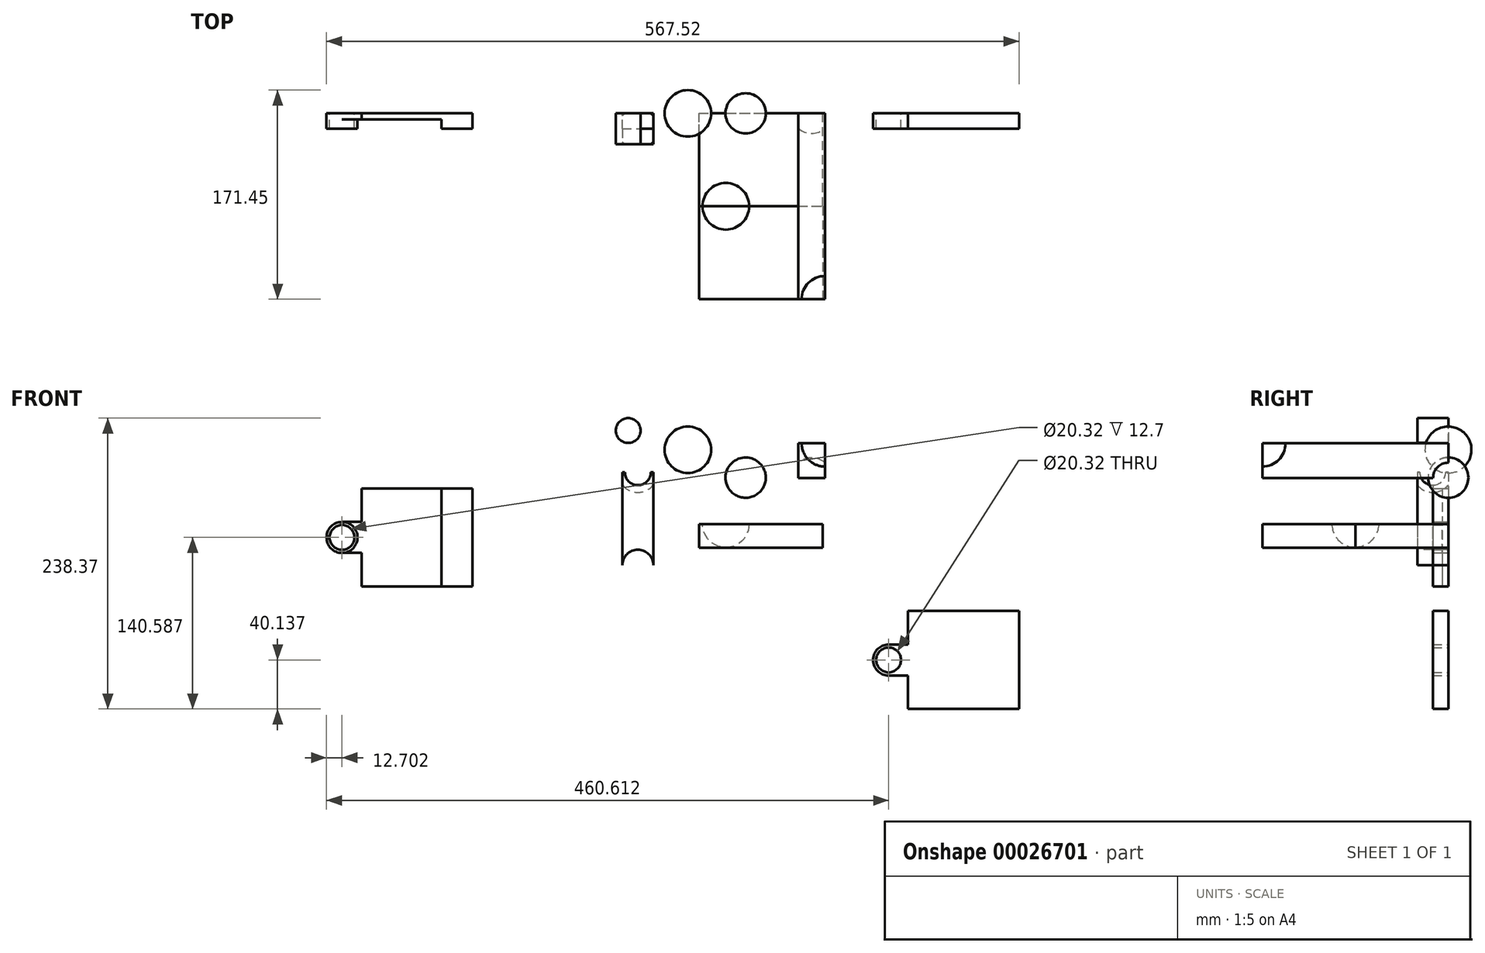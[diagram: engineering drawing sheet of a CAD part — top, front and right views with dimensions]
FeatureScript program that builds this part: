
annotation { "Feature Type Name" : "Feature", "Feature Type Description" : "" }
export const myFeature = defineFeature(function(context is Context, id is Id, definition is map)
    precondition{}
    {
        {
            var Q0;
            Q0=qCreatedBy(makeId("Front.planeOp"),FACE);
            var sketch = newSketch(context, id + "F0", { "sketchPlane" : qUnion([Q0])});
            skLineSegment(sketch, "E0.bottom", {"start": v(-45.9, -18.33) * mm, "end": v(55.43, -18.33) * mm});
            skLineSegment(sketch, "E0.top", {"start": v(-45.9, -37.7) * mm, "end": v(55.43, -37.7) * mm});
            skLineSegment(sketch, "E0.left", {"start": v(-45.9, -18.33) * mm, "end": v(-45.9, -37.7) * mm});
            skLineSegment(sketch, "E0.right", {"start": v(55.43, -18.33) * mm, "end": v(55.43, -37.7) * mm});
            skSolve(sketch);
        }
        {
            var Q0;
            Q0=makeQuery(id+"F0.imprint","IMPRINT",FACE,{"disambiguationData":[TD([[makeQuery(id+"F0.imprint","IMPRINT",EDGE,{"derivedFrom":sQuery(id+"F0.wireOp",EDGE,"E0.bottom")}),-1.0]])]});
            extrude(context, id + "F1", {"entities" : qUnion([Q0]), "depth" : 76.2 * mm});
        }
        {
            var Q0;
            Q0=makeQuery(id+"F1.opExtrude","SWEPT_FACE",FACE,{"disambiguationData":[OSD([sQuery(id+"F0.wireOp",EDGE,"E0.bottom")])]});
            var sketch = newSketch(context, id + "F2", { "sketchPlane" : qUnion([Q0])});
            skCircle(sketch, "E1", {"center": v(0, -38.64) * mm, "radius": 20.55 * mm});
            skSolve(sketch);
        }
        {
            var Q0;
            Q0=qCreatedBy(makeId("Front.planeOp"),FACE);
            var sketch = newSketch(context, id + "F3", { "sketchPlane" : qUnion([Q0])});
            skCircle(sketch, "E2", {"center": v(-55.13, 42.52) * mm, "radius": 19.05 * mm});
            skLineSegment(sketch, "E3", {"start": v(-55.13, 72.76) * mm, "end": v(-55.13, 3.83) * mm});
            skSolve(sketch);
        }
        {
            var Q0;
            {var subQ0=sQuery(id+"F3.wireOp",EDGE,"E3");var subQ1=sQuery(id+"F3.wireOp",EDGE,"E2");var subQ3=makeQuery(id+"F3.imprint","INTERSECT",VERTEX,{"disambiguationData":[OD(0.0)],"derivedFrom":[subQ1,subQ0]});Q0=makeQuery(id+"F3.imprint","IMPRINT",FACE,{"disambiguationData":[TD([[makeQuery(id+"F3.imprint","IMPRINT",EDGE,{"disambiguationData":[TD([[subQ3,-1.0]])],"derivedFrom":subQ1}),1.0]])]});}
            var Q1;
            Q1=sQuery(id+"F3.wireOp",EDGE,"E3");
            revolve(context, id + "F4", {"entities" : qUnion([Q0]), "axis" : qUnion([Q1]), "revolveType" : RevolveType.FULL});
        }
        {
            var Q0;
            Q0=makeQuery(id+"F2.imprint","IMPRINT",FACE,{"disambiguationData":[TD([[makeQuery(id+"F2.imprint","IMPRINT",EDGE,{"derivedFrom":sQuery(id+"F2.wireOp",EDGE,"E1")}),-1.0]])]});
            var sketch = newSketch(context, id + "F5", { "sketchPlane" : qUnion([Q0])});
            skCircle(sketch, "E4", {"center": v(-24.04, -76.13) * mm, "radius": 19.05 * mm});
            skLineSegment(sketch, "E5", {"start": v(-5, -76.21) * mm, "end": v(-43.1, -76.21) * mm});
            skSolve(sketch);
        }
        {
            var Q0;
            {var subQ0=makeQuery(id+"F2.imprint","IMPRINT",EDGE,{"derivedFrom":makeQuery(id+"F1.opExtrude","CAP_EDGE",EDGE,{"disambiguationData":[OSD([sQuery(id+"F0.wireOp",EDGE,"E0.bottom")])],"isStart":false})});var subQ1=sQuery(id+"F5.wireOp",EDGE,"E4");var subQ3=makeQuery(id+"F5.imprint","INTERSECT",VERTEX,{"disambiguationData":[OD(0.0)],"derivedFrom":[subQ0,subQ1]});Q0=makeQuery(id+"F5.imprint","IMPRINT",FACE,{"disambiguationData":[TD([[makeQuery(id+"F5.imprint","IMPRINT",EDGE,{"disambiguationData":[TD([[subQ3,1.0]])],"derivedFrom":subQ1}),1.0]])]});}
            var Q1;
            Q1=sQuery(id+"F5.wireOp",EDGE,"E5");
            revolve(context, id + "F6", {"operationType" : NewBodyOperationType.REMOVE, "entities" : qUnion([Q0]), "axis" : qUnion([Q1]), "revolveType" : RevolveType.FULL, "oppositeDirection" : true});
        }
        {
            var Q0;
            Q0=qCreatedBy(makeId("Front.planeOp"),FACE);
            var sketch = newSketch(context, id + "F7", { "sketchPlane" : qUnion([Q0])});
            skLineSegment(sketch, "E6.bottom", {"start": v(35.46, 47.83) * mm, "end": v(57.21, 47.83) * mm});
            skLineSegment(sketch, "E6.top", {"start": v(35.46, 19.52) * mm, "end": v(57.21, 19.52) * mm});
            skLineSegment(sketch, "E6.left", {"start": v(35.46, 47.83) * mm, "end": v(35.46, 19.52) * mm});
            skLineSegment(sketch, "E6.right", {"start": v(57.21, 47.83) * mm, "end": v(57.21, 19.52) * mm});
            skSolve(sketch);
        }
        {
            var Q0;
            Q0=makeQuery(id+"F7.imprint","IMPRINT",FACE,{"disambiguationData":[TD([[makeQuery(id+"F7.imprint","IMPRINT",EDGE,{"derivedFrom":sQuery(id+"F7.wireOp",EDGE,"E6.bottom")}),-1.0]])]});
            extrude(context, id + "F8", {"entities" : qUnion([Q0]), "depth" : 152.4 * mm});
        }
        {
            var Q0;
            Q0=makeQuery(id+"F8.opExtrude","SWEPT_FACE",FACE,{"disambiguationData":[OSD([sQuery(id+"F7.wireOp",EDGE,"E6.bottom")])]});
            var sketch = newSketch(context, id + "F9", { "sketchPlane" : qUnion([Q0])});
            skCircle(sketch, "E7", {"center": v(57.21, -152.4) * mm, "radius": 19.05 * mm});
            skLineSegment(sketch, "E8", {"start": v(39.58, -159.61) * mm, "end": v(74.85, -145.19) * mm});
            skSolve(sketch);
        }
        {
            var Q0;
            Q0=makeQuery(id+"F1.opExtrude","SWEPT_BODY",BODY,{"disambiguationData":[OSD([sQuery(id+"F0.wireOp",EDGE,"E0.bottom"),sQuery(id+"F0.wireOp",EDGE,"E0.top"),sQuery(id+"F0.wireOp",EDGE,"E0.left"),sQuery(id+"F0.wireOp",EDGE,"E0.right")])]});
            var Q1;
            Q1=makeQuery(id+"F1.opExtrude","CAP_FACE",FACE,{"disambiguationData":[OSD([sQuery(id+"F0.wireOp",EDGE,"E0.bottom"),sQuery(id+"F0.wireOp",EDGE,"E0.top"),sQuery(id+"F0.wireOp",EDGE,"E0.left"),sQuery(id+"F0.wireOp",EDGE,"E0.right")])],"isStart":false});
            mirror(context, id + "F10", {"operationType" : NewBodyOperationType.ADD, "entities" : qUnion([Q0]), "mirrorPlane" : qUnion([Q1])});
        }
        {
            var Q0;
            Q0=makeQuery(id+"F8.opExtrude","CAP_FACE",FACE,{"disambiguationData":[OSD([sQuery(id+"F7.wireOp",EDGE,"E6.bottom"),sQuery(id+"F7.wireOp",EDGE,"E6.top"),sQuery(id+"F7.wireOp",EDGE,"E6.left"),sQuery(id+"F7.wireOp",EDGE,"E6.right")])],"isStart":true});
            var sketch = newSketch(context, id + "F11", { "sketchPlane" : qUnion([Q0])});
            skCircle(sketch, "E9", {"center": v(-46.34, 19.52) * mm, "radius": 16.51 * mm});
            skSolve(sketch);
        }
        {
            var Q0;
            {var subQ3=makeQuery(id+"F8.opExtrude","CAP_EDGE",EDGE,{"disambiguationData":[OSD([sQuery(id+"F7.wireOp",EDGE,"E6.top")])],"isStart":true});Q0=makeQuery(id+"F11.imprint","IMPRINT",FACE,{"disambiguationData":[TD([[makeQuery(id+"F11.imprint","IMPRINT",EDGE,{"derivedFrom":subQ3}),-1.0]])]});}
            var Q1;
            Q1=makeQuery(id+"F8.opExtrude","CAP_EDGE",EDGE,{"disambiguationData":[OSD([sQuery(id+"F7.wireOp",EDGE,"E6.top")])],"isStart":true});
            revolve(context, id + "F12", {"operationType" : NewBodyOperationType.REMOVE, "entities" : qUnion([Q0]), "axis" : qUnion([Q1]), "revolveType" : RevolveType.FULL, "oppositeDirection" : true});
        }
        {
            var Q0;
            Q0=qCreatedBy(makeId("Front.planeOp"),FACE);
            var sketch = newSketch(context, id + "F13", { "sketchPlane" : qUnion([Q0])});
            skCircle(sketch, "E10", {"center": v(-7.76, 19.72) * mm, "radius": 16.51 * mm});
            skLineSegment(sketch, "E11", {"start": v(4.05, 31.26) * mm, "end": v(-19.57, 8.18) * mm});
            skSolve(sketch);
        }
        {
            var Q0;
            {var subQ0=sQuery(id+"F13.wireOp",EDGE,"E11");Q0=makeQuery(id+"F13.imprint","IMPRINT",FACE,{"disambiguationData":[TD([[makeQuery(id+"F13.imprint","IMPRINT",EDGE,{"derivedFrom":subQ0}),-1.0]])]});}
            var Q1;
            Q1=sQuery(id+"F13.wireOp",EDGE,"E11");
            revolve(context, id + "F14", {"entities" : qUnion([Q0]), "axis" : qUnion([Q1]), "revolveType" : RevolveType.FULL});
        }
        {
            var Q0;
            Q0=qCreatedBy(makeId("Front.planeOp"),FACE);
            var sketch = newSketch(context, id + "F15", { "sketchPlane" : qUnion([Q0])});
            skLineSegment(sketch, "E12.bottom", {"start": v(-108.83, 24.17) * mm, "end": v(-83.43, 24.17) * mm});
            skLineSegment(sketch, "E12.top", {"start": v(-108.83, -52.03) * mm, "end": v(-83.43, -52.03) * mm});
            skLineSegment(sketch, "E12.left", {"start": v(-108.83, 24.17) * mm, "end": v(-108.83, -52.03) * mm});
            skLineSegment(sketch, "E12.right", {"start": v(-83.43, 24.17) * mm, "end": v(-83.43, -52.03) * mm});
            skSolve(sketch);
        }
        {
            var Q0;
            Q0=makeQuery(id+"F15.imprint","IMPRINT",FACE,{"disambiguationData":[TD([[makeQuery(id+"F15.imprint","IMPRINT",EDGE,{"derivedFrom":sQuery(id+"F15.wireOp",EDGE,"E12.bottom")}),-1.0]])]});
            extrude(context, id + "F16", {"entities" : qUnion([Q0]), "depth" : 12.7 * mm});
        }
        {
            var Q0;
            Q0=makeQuery(id+"F16.opExtrude","CAP_FACE",FACE,{"disambiguationData":[OSD([sQuery(id+"F15.wireOp",EDGE,"E12.bottom"),sQuery(id+"F15.wireOp",EDGE,"E12.top"),sQuery(id+"F15.wireOp",EDGE,"E12.left"),sQuery(id+"F15.wireOp",EDGE,"E12.right")])],"isStart":false});
            var sketch = newSketch(context, id + "F17", { "sketchPlane" : qUnion([Q0])});
            skCircle(sketch, "E13", {"center": v(-96.13, 24.17) * mm, "radius": 16.55 * mm});
            skSolve(sketch);
        }
        {
            var Q0;
            {var subQ3=makeQuery(id+"F16.opExtrude","CAP_EDGE",EDGE,{"disambiguationData":[OSD([sQuery(id+"F15.wireOp",EDGE,"E12.bottom")])],"isStart":false});Q0=makeQuery(id+"F17.imprint","IMPRINT",FACE,{"disambiguationData":[TD([[makeQuery(id+"F17.imprint","IMPRINT",EDGE,{"derivedFrom":subQ3}),-1.0]])]});}
            var Q1;
            Q1=makeQuery(id+"F16.opExtrude","CAP_EDGE",EDGE,{"disambiguationData":[OSD([sQuery(id+"F15.wireOp",EDGE,"E12.bottom")])],"isStart":false});
            revolve(context, id + "F18", {"operationType" : NewBodyOperationType.REMOVE, "entities" : qUnion([Q0]), "axis" : qUnion([Q1]), "revolveType" : RevolveType.FULL, "oppositeDirection" : true});
        }
        {
            var Q0;
            Q0=makeQuery(id+"F16.opExtrude","SWEPT_BODY",BODY,{"disambiguationData":[OSD([sQuery(id+"F15.wireOp",EDGE,"E12.bottom"),sQuery(id+"F15.wireOp",EDGE,"E12.top"),sQuery(id+"F15.wireOp",EDGE,"E12.left"),sQuery(id+"F15.wireOp",EDGE,"E12.right")])]});
            var Q1;
            Q1=makeQuery(id+"F16.opExtrude","CAP_FACE",FACE,{"disambiguationData":[OSD([sQuery(id+"F15.wireOp",EDGE,"E12.bottom"),sQuery(id+"F15.wireOp",EDGE,"E12.top"),sQuery(id+"F15.wireOp",EDGE,"E12.left"),sQuery(id+"F15.wireOp",EDGE,"E12.right")])],"isStart":false});
            mirror(context, id + "F19", {"operationType" : NewBodyOperationType.ADD, "entities" : qUnion([Q0]), "mirrorPlane" : qUnion([Q1])});
        }
        {
            var Q0;
            Q0=makeQuery(id+"F19.opPattern","COPY",FACE,{"derivedFrom":makeQuery(id+"F16.opExtrude","CAP_FACE",FACE,{"disambiguationData":[OSD([sQuery(id+"F15.wireOp",EDGE,"E12.bottom"),sQuery(id+"F15.wireOp",EDGE,"E12.top"),sQuery(id+"F15.wireOp",EDGE,"E12.left"),sQuery(id+"F15.wireOp",EDGE,"E12.right")])],"isStart":true}),"instanceName":"1"});
            var sketch = newSketch(context, id + "F20", { "sketchPlane" : qUnion([Q0])});
            skCircle(sketch, "E14", {"center": v(-96.13, -52.03) * mm, "radius": 12.7 * mm});
            skSolve(sketch);
        }
        {
            var Q0;
            {var subQ3=makeQuery(id+"F19.opPattern","COPY",EDGE,{"derivedFrom":makeQuery(id+"F16.opExtrude","CAP_EDGE",EDGE,{"disambiguationData":[OSD([sQuery(id+"F15.wireOp",EDGE,"E12.top")])],"isStart":true}),"instanceName":"1"});Q0=makeQuery(id+"F20.imprint","IMPRINT",FACE,{"disambiguationData":[TD([[makeQuery(id+"F20.imprint","IMPRINT",EDGE,{"derivedFrom":subQ3}),1.0]])]});}
            extrude(context, id + "F21", {"entities" : qUnion([Q0]), "operationType" : NewBodyOperationType.REMOVE, "oppositeDirection" : true, "depth" : 25.4 * mm});
        }
        {
            var Q0;
            Q0=qCreatedBy(makeId("Front.planeOp"),FACE);
            var sketch = newSketch(context, id + "F22", { "sketchPlane" : qUnion([Q0])});
            skCircle(sketch, "E15", {"center": v(-104.02, 58.31) * mm, "radius": 10.16 * mm});
            skSolve(sketch);
        }
        {
            var Q0;
            Q0=makeQuery(id+"F22.imprint","IMPRINT",FACE,{"disambiguationData":[TD([[makeQuery(id+"F22.imprint","IMPRINT",EDGE,{"derivedFrom":sQuery(id+"F22.wireOp",EDGE,"E15")}),1.0]])]});
            extrude(context, id + "F23", {"entities" : qUnion([Q0]), "depth" : 25.4 * mm});
        }
        {
            var Q0;
            Q0=qCreatedBy(makeId("Front.planeOp"),FACE);
            var sketch = newSketch(context, id + "F24", { "sketchPlane" : qUnion([Q0])});
            skArc(sketch, "E16", {"start": v(186.05, 20.7) * mm, "mid": v(184.13, 83.94) * mm, "end": v(123.22, 66.83) * mm});
            skSolve(sketch);
        }
        {
            var Q0;
            Q0=sQuery(id+"F24.wireOp",EDGE,"E16");
            extrude(context, id + "F25", {"bodyType" : ToolBodyType.SURFACE, "surfaceEntities" : qUnion([Q0]), "depth" : 25.4 * mm});
        }
        {
            var Q0;
            Q0=qCreatedBy(makeId("Front.planeOp"),FACE);
            var sketch = newSketch(context, id + "F26", { "sketchPlane" : qUnion([Q0])});
            skArc(sketch, "E17", {"start": v(-158.41, -137.84) * mm, "mid": v(-171.84, -76.25) * mm, "end": v(-231.9, -57.09) * mm});
            skSolve(sketch);
        }
        {
            var Q0;
            Q0=sQuery(id+"F26.wireOp",EDGE,"E17");
            extrude(context, id + "F27", {"bodyType" : ToolBodyType.SURFACE, "surfaceEntities" : qUnion([Q0]), "depth" : 25.4 * mm});
        }
        {
            var Q0;
            {var subQ0=sQuery(id+"F7.wireOp",EDGE,"E6.bottom");var subQ1=makeQuery(id+"F8.opExtrude","CAP_EDGE",EDGE,{"disambiguationData":[OSD([subQ0])],"isStart":false});var subQ2=sQuery(id+"F9.wireOp",EDGE,"E7");var subQ3=makeQuery(id+"F9.imprint","INTERSECT",VERTEX,{"derivedFrom":[subQ1,subQ2]});Q0=makeQuery(id+"F9.imprint","IMPRINT",FACE,{"disambiguationData":[TD([[makeQuery(id+"F9.imprint","IMPRINT",EDGE,{"disambiguationData":[TD([[subQ3,1.0]])],"derivedFrom":subQ2}),1.0]])]});}
            var Q1;
            {var subQ2=sQuery(id+"F9.wireOp",EDGE,"E7");var subQ4=sQuery(id+"F9.wireOp",EDGE,"E8");var subQ6=makeQuery(id+"F9.imprint","INTERSECT",VERTEX,{"disambiguationData":[OD(0.0)],"derivedFrom":[subQ2,subQ4]});Q1=makeQuery(id+"F9.imprint","IMPRINT",FACE,{"disambiguationData":[TD([[makeQuery(id+"F9.imprint","IMPRINT",EDGE,{"disambiguationData":[TD([[subQ6,1.0]])],"derivedFrom":subQ2}),1.0]])]});}
            var Q2;
            {var subQ2=sQuery(id+"F9.wireOp",EDGE,"E7");var subQ4=sQuery(id+"F9.wireOp",EDGE,"E8");var subQ6=makeQuery(id+"F9.imprint","INTERSECT",VERTEX,{"disambiguationData":[OD(1.0)],"derivedFrom":[subQ2,subQ4]});Q2=makeQuery(id+"F9.imprint","IMPRINT",FACE,{"disambiguationData":[TD([[makeQuery(id+"F9.imprint","IMPRINT",EDGE,{"disambiguationData":[TD([[subQ6,-1.0]])],"derivedFrom":subQ2}),1.0]])]});}
            var Q3;
            Q3=sQuery(id+"F9.wireOp",EDGE,"E8");
            revolve(context, id + "F28", {"operationType" : NewBodyOperationType.REMOVE, "entities" : qUnion([Q0, Q1, Q2]), "axis" : qUnion([Q3]), "revolveType" : RevolveType.FULL, "oppositeDirection" : true});
        }
        {
            var Q0;
            Q0=qCreatedBy(makeId("Front.planeOp"),FACE);
            var sketch = newSketch(context, id + "F29", { "sketchPlane" : qUnion([Q0])});
            skLineSegment(sketch, "E18.bottom", {"start": v(109.36, -117.06) * mm, "end": v(161.15, -117.06) * mm});
            skLineSegment(sketch, "E18.top", {"start": v(109.36, -142.46) * mm, "end": v(161.15, -142.46) * mm});
            skLineSegment(sketch, "E18.left", {"start": v(109.36, -117.06) * mm, "end": v(109.36, -142.46) * mm});
            skLineSegment(sketch, "E18.right", {"start": v(161.15, -117.06) * mm, "end": v(161.15, -142.46) * mm});
            skCircle(sketch, "E19", {"center": v(109.36, -129.76) * mm, "radius": 12.7 * mm});
            skCircle(sketch, "E20", {"center": v(109.36, -129.76) * mm, "radius": 10.16 * mm});
            skLineSegment(sketch, "E21", {"start": v(125.36, -117.06) * mm, "end": v(125.36, -89.63) * mm});
            skLineSegment(sketch, "E22", {"start": v(125.36, -89.63) * mm, "end": v(216.27, -89.63) * mm});
            skLineSegment(sketch, "E23", {"start": v(216.27, -89.63) * mm, "end": v(216.27, -169.9) * mm});
            skLineSegment(sketch, "E24", {"start": v(216.27, -169.9) * mm, "end": v(125.36, -169.9) * mm});
            skLineSegment(sketch, "E25", {"start": v(125.36, -169.9) * mm, "end": v(125.36, -142.46) * mm});
            skSolve(sketch);
        }
        {
            var Q0;
            {var subQ0=sQuery(id+"F29.wireOp",EDGE,"E20");var subQ1=sQuery(id+"F29.wireOp",EDGE,"E18.left");var subQ3=makeQuery(id+"F29.imprint","INTERSECT",VERTEX,{"disambiguationData":[OD(0.0)],"derivedFrom":[subQ1,subQ0]});Q0=makeQuery(id+"F29.imprint","IMPRINT",FACE,{"disambiguationData":[TD([[makeQuery(id+"F29.imprint","IMPRINT",EDGE,{"disambiguationData":[TD([[subQ3,1.0]])],"derivedFrom":subQ0}),-1.0]])]});}
            var Q1;
            {var subQ0=sQuery(id+"F29.wireOp",EDGE,"E20");var subQ1=sQuery(id+"F29.wireOp",EDGE,"E18.left");var subQ3=makeQuery(id+"F29.imprint","INTERSECT",VERTEX,{"disambiguationData":[OD(0.0)],"derivedFrom":[subQ1,subQ0]});Q1=makeQuery(id+"F29.imprint","IMPRINT",FACE,{"disambiguationData":[TD([[makeQuery(id+"F29.imprint","IMPRINT",EDGE,{"disambiguationData":[TD([[subQ3,-1.0]])],"derivedFrom":subQ0}),-1.0]])]});}
            var Q2;
            {var subQ3=sQuery(id+"F29.wireOp",EDGE,"E18.bottom");Q2=makeQuery(id+"F29.imprint","IMPRINT",FACE,{"disambiguationData":[TD([[makeQuery(id+"F29.imprint","IMPRINT",EDGE,{"derivedFrom":subQ3}),-1.0]])]});}
            var Q3;
            {var subQ2=sQuery(id+"F29.wireOp",EDGE,"E18.right");Q3=makeQuery(id+"F29.imprint","IMPRINT",FACE,{"disambiguationData":[TD([[makeQuery(id+"F29.imprint","IMPRINT",EDGE,{"derivedFrom":subQ2}),1.0]])]});}
            extrude(context, id + "F30", {"entities" : qUnion([Q0, Q1, Q2, Q3]), "depth" : 12.7 * mm});
        }
        {
            var Q0;
            Q0=qCreatedBy(makeId("Front.planeOp"),FACE);
            var sketch = newSketch(context, id + "F31", { "sketchPlane" : qUnion([Q0])});
            skLineSegment(sketch, "E26.bottom", {"start": v(-338.55, -16.61) * mm, "end": v(-322.55, -16.61) * mm});
            skLineSegment(sketch, "E26.top", {"start": v(-338.55, -42.01) * mm, "end": v(-322.55, -42.01) * mm});
            skLineSegment(sketch, "E26.left", {"start": v(-338.55, -16.61) * mm, "end": v(-338.55, -42.01) * mm});
            skLineSegment(sketch, "E26.right", {"start": v(-322.55, -16.61) * mm, "end": v(-322.55, -42.01) * mm});
            skLineSegment(sketch, "E27.bottom", {"start": v(-322.55, 10.82) * mm, "end": v(-231.64, 10.82) * mm});
            skLineSegment(sketch, "E27.top", {"start": v(-322.55, -69.44) * mm, "end": v(-231.64, -69.44) * mm});
            skLineSegment(sketch, "E27.left", {"start": v(-322.55, 10.82) * mm, "end": v(-322.55, -69.44) * mm});
            skLineSegment(sketch, "E27.right", {"start": v(-231.64, 10.82) * mm, "end": v(-231.64, -69.44) * mm});
            skCircle(sketch, "E28", {"center": v(-338.55, -29.31) * mm, "radius": 12.7 * mm});
            skCircle(sketch, "E29", {"center": v(-338.55, -29.31) * mm, "radius": 10.16 * mm});
            skSolve(sketch);
        }
        {
            var Q0;
            {var subQ0=sQuery(id+"F31.wireOp",EDGE,"E29");var subQ1=sQuery(id+"F31.wireOp",EDGE,"E26.left");var subQ3=makeQuery(id+"F31.imprint","INTERSECT",VERTEX,{"disambiguationData":[OD(0.0)],"derivedFrom":[subQ1,subQ0]});Q0=makeQuery(id+"F31.imprint","IMPRINT",FACE,{"disambiguationData":[TD([[makeQuery(id+"F31.imprint","IMPRINT",EDGE,{"disambiguationData":[TD([[subQ3,-1.0]])],"derivedFrom":subQ0}),-1.0]])]});}
            var Q1;
            {var subQ0=sQuery(id+"F31.wireOp",EDGE,"E29");var subQ1=sQuery(id+"F31.wireOp",EDGE,"E26.left");var subQ3=makeQuery(id+"F31.imprint","INTERSECT",VERTEX,{"disambiguationData":[OD(0.0)],"derivedFrom":[subQ1,subQ0]});Q1=makeQuery(id+"F31.imprint","IMPRINT",FACE,{"disambiguationData":[TD([[makeQuery(id+"F31.imprint","IMPRINT",EDGE,{"disambiguationData":[TD([[subQ3,1.0]])],"derivedFrom":subQ0}),-1.0]])]});}
            extrude(context, id + "F32", {"entities" : qUnion([Q0, Q1]), "depth" : 12.7 * mm});
        }
        {
            var Q0;
            Q0 = qSketchRegion(id + "F31", true);
            extrude(context, id + "F33", {"entities" : qUnion([Q0]), "operationType" : NewBodyOperationType.ADD, "depth" : 5.08 * mm});
        }
        {
            var Q0;
            Q0=makeQuery(id+"F33.opExtrude","CAP_FACE",FACE,{"disambiguationData":[OSD([sQuery(id+"F31.wireOp",EDGE,"E26.bottom"),sQuery(id+"F31.wireOp",EDGE,"E26.top"),sQuery(id+"F31.wireOp",EDGE,"E27.bottom"),sQuery(id+"F31.wireOp",EDGE,"E27.top"),sQuery(id+"F31.wireOp",EDGE,"E27.left"),sQuery(id+"F31.wireOp",EDGE,"E27.right"),sQuery(id+"F31.wireOp",EDGE,"E28"),sQuery(id+"F31.wireOp",EDGE,"E29")])],"isStart":false});
            var sketch = newSketch(context, id + "F34", { "sketchPlane" : qUnion([Q0])});
            skLineSegment(sketch, "E30.bottom", {"start": v(-231.64, 10.82) * mm, "end": v(-257.02, 10.82) * mm});
            skLineSegment(sketch, "E30.top", {"start": v(-231.64, -69.44) * mm, "end": v(-257.02, -69.44) * mm});
            skLineSegment(sketch, "E30.left", {"start": v(-231.64, 10.82) * mm, "end": v(-231.64, -69.44) * mm});
            skLineSegment(sketch, "E30.right", {"start": v(-257.02, 10.82) * mm, "end": v(-257.02, -69.44) * mm});
            skSolve(sketch);
        }
        {
            var Q0;
            Q0=makeQuery(id+"F34.imprint","IMPRINT",FACE,{"disambiguationData":[TD([[makeQuery(id+"F34.imprint","IMPRINT",EDGE,{"derivedFrom":sQuery(id+"F34.wireOp",EDGE,"E30.bottom")}),-1.0]])]});
            extrude(context, id + "F35", {"entities" : qUnion([Q0]), "operationType" : NewBodyOperationType.ADD, "depth" : 7.62 * mm});
        }
    });
